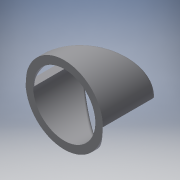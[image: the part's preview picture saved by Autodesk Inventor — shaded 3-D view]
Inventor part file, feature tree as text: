
AUTODESK INVENTOR PART (.ipt)
format: ipt  version: 2018 (Build 220112000, 112)  size: 231,424 bytes
history: native  units: mm
features: extrude x2, sketch x2, pattern_circular x1, fillet x1
ambient origin geometry x8: Origin, YZ Plane, XZ Plane, XY Plane, X Axis, Y Axis, Z Axis, Center Point
bodies: Solide1 (feature_tree)
feature tree (6):
  extrude  "Extrusion1"  Depth=22.5mm
  extrude  "Extrusion2"  Depth=28.0mm
  pattern_circular  "Réseau circulaire1"  Count=2  [1 undecoded]
  fillet  "Congé1"  [1 undecoded]
  sketch  "Esquisse1"
  sketch  "Esquisse6"
note: 2 required parameter values undecoded (feature->parameter linkage not recoverable at this tier; creation-order binding heuristic only, values carry confidence <= 0.55)
